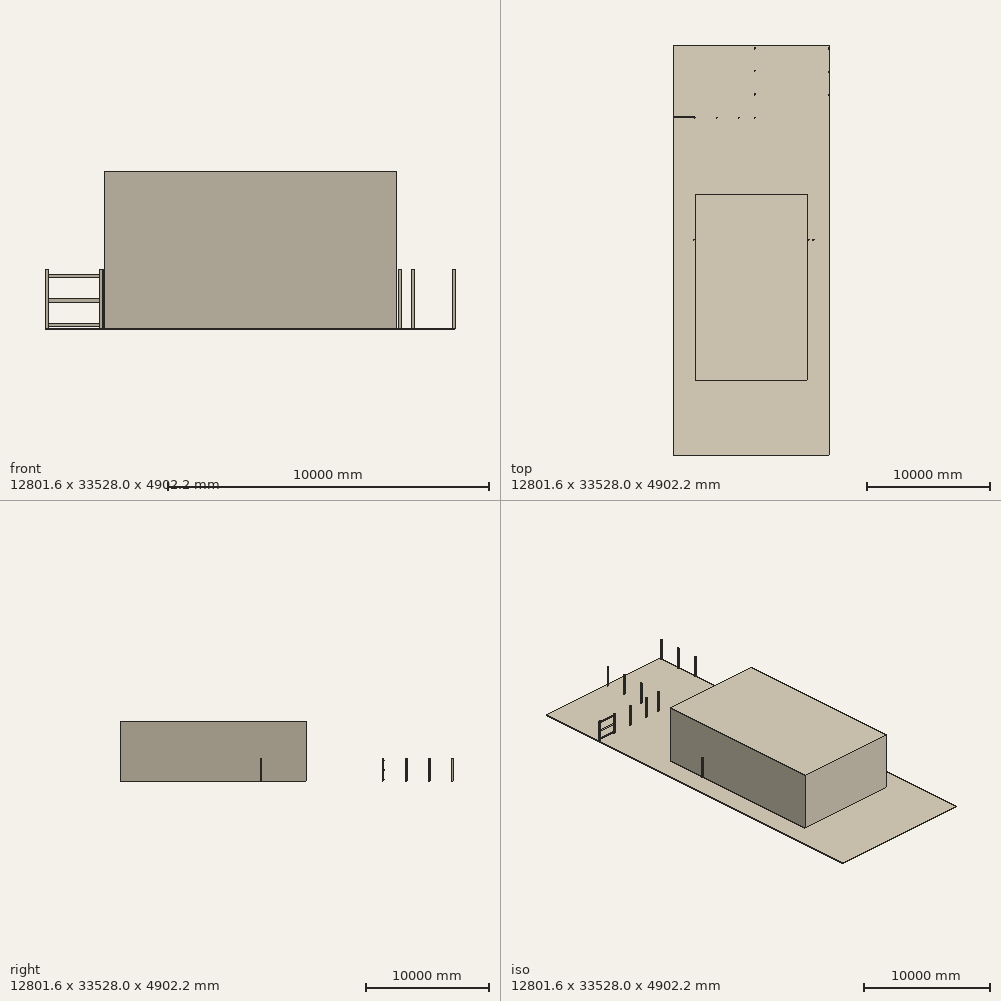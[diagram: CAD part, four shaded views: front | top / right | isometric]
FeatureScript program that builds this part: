
annotation { "Feature Type Name" : "Feature", "Feature Type Description" : "" }
export const myFeature = defineFeature(function(context is Context, id is Id, definition is map)
    precondition{}
    {
        {
            var Q0;
            Q0=qCreatedBy(makeId("Top.planeOp"),FACE);
            var sketch = newSketch(context, id + "F0", { "sketchPlane" : qUnion([Q0])});
            skLineSegment(sketch, "E0", {"start": v(-6400.8, 16764) * mm, "end": v(6400.8, 16764) * mm});
            skLineSegment(sketch, "E1", {"start": v(-6400.8, 16764) * mm, "end": v(-6400.8, -16764) * mm});
            skLineSegment(sketch, "E2", {"start": v(-6400.8, -16764) * mm, "end": v(6400.8, -16764) * mm});
            skLineSegment(sketch, "E3", {"start": v(6400.8, -16764) * mm, "end": v(6400.8, 16764) * mm});
            skLineSegment(sketch, "E4", {"start": v(0, -16764) * mm, "end": v(0, 16764) * mm, "construction": true});
            skSolve(sketch);
        }
        {
            var Q0;
            Q0 = qSketchRegion(id + "F0", true);
            extrude(context, id + "F1", {"entities" : qUnion([Q0]), "depth" : 25.4 * mm, "offsetDistance" : 25.4 * mm});
        }
        {
            var Q0;
            Q0=makeQuery(id+"F1.opExtrude","CAP_FACE",FACE,{"disambiguationData":[OSD([sQuery(id+"F0.wireOp",EDGE,"E0"),sQuery(id+"F0.wireOp",EDGE,"E1"),sQuery(id+"F0.wireOp",EDGE,"E2"),sQuery(id+"F0.wireOp",EDGE,"E3")])],"isStart":false});
            var sketch = newSketch(context, id + "F2", { "sketchPlane" : qUnion([Q0])});
            skLineSegment(sketch, "E5.bottom", {"start": v(-4572, 4572) * mm, "end": v(4572, 4572) * mm});
            skLineSegment(sketch, "E5.top", {"start": v(-4572, -10668) * mm, "end": v(4572, -10668) * mm});
            skLineSegment(sketch, "E5.left", {"start": v(-4572, 4572) * mm, "end": v(-4572, -10668) * mm});
            skLineSegment(sketch, "E5.right", {"start": v(4572, 4572) * mm, "end": v(4572, -10668) * mm});
            skSolve(sketch);
        }
        {
            var Q0;
            Q0 = qSketchRegion(id + "F2", true);
            extrude(context, id + "F3", {"entities" : qUnion([Q0]), "depth" : 4876.8 * mm, "offsetDistance" : 25.4 * mm});
        }
        {
            var Q0;
            Q0=makeQuery(id+"F1.opExtrude","CAP_FACE",FACE,{"disambiguationData":[OSD([sQuery(id+"F0.wireOp",EDGE,"E0"),sQuery(id+"F0.wireOp",EDGE,"E1"),sQuery(id+"F0.wireOp",EDGE,"E2"),sQuery(id+"F0.wireOp",EDGE,"E3")])],"isStart":false});
            var sketch = newSketch(context, id + "F4", { "sketchPlane" : qUnion([Q0])});
            skLineSegment(sketch, "E6.bottom", {"start": v(-6400.8, 10769.6) * mm, "end": v(-6299.2, 10769.6) * mm});
            skLineSegment(sketch, "E6.top", {"start": v(-6400.8, 10871.2) * mm, "end": v(-6299.2, 10871.2) * mm});
            skLineSegment(sketch, "E6.left", {"start": v(-6400.8, 10769.6) * mm, "end": v(-6400.8, 10871.2) * mm});
            skLineSegment(sketch, "E6.right", {"start": v(-6299.2, 10769.6) * mm, "end": v(-6299.2, 10871.2) * mm});
            skLineSegment(sketch, "E7.bottom", {"start": v(-4690.53, 10769.6) * mm, "end": v(-4588.93, 10769.6) * mm});
            skLineSegment(sketch, "E7.top", {"start": v(-4690.53, 10871.2) * mm, "end": v(-4588.93, 10871.2) * mm});
            skLineSegment(sketch, "E7.left", {"start": v(-4690.53, 10769.6) * mm, "end": v(-4690.53, 10871.2) * mm});
            skLineSegment(sketch, "E7.right", {"start": v(-4588.93, 10769.6) * mm, "end": v(-4588.93, 10871.2) * mm});
            skLineSegment(sketch, "E8.bottom", {"start": v(254, 10769.6) * mm, "end": v(355.6, 10769.6) * mm});
            skLineSegment(sketch, "E8.top", {"start": v(254, 10871.2) * mm, "end": v(355.6, 10871.2) * mm});
            skLineSegment(sketch, "E8.left", {"start": v(254, 10769.6) * mm, "end": v(254, 10871.2) * mm});
            skLineSegment(sketch, "E8.right", {"start": v(355.6, 10769.6) * mm, "end": v(355.6, 10871.2) * mm});
            skLineSegment(sketch, "E9.bottom", {"start": v(254, 14630.4) * mm, "end": v(355.6, 14630.4) * mm});
            skLineSegment(sketch, "E9.top", {"start": v(254, 14732) * mm, "end": v(355.6, 14732) * mm});
            skLineSegment(sketch, "E9.left", {"start": v(254, 14630.4) * mm, "end": v(254, 14732) * mm});
            skLineSegment(sketch, "E9.right", {"start": v(355.6, 14630.4) * mm, "end": v(355.6, 14732) * mm});
            skLineSegment(sketch, "E10", {"start": v(-6350, 10871.2) * mm, "end": v(-4639.73, 10871.2) * mm, "construction": true});
            skLineSegment(sketch, "E11", {"start": v(304.8, 10871.2) * mm, "end": v(304.8, 12700) * mm, "construction": true});
            skLineSegment(sketch, "E12.bottom", {"start": v(6299.2, 16459.2) * mm, "end": v(6400.8, 16459.2) * mm});
            skLineSegment(sketch, "E12.top", {"start": v(6299.2, 16560.8) * mm, "end": v(6400.8, 16560.8) * mm});
            skLineSegment(sketch, "E12.left", {"start": v(6299.2, 16459.2) * mm, "end": v(6299.2, 16560.8) * mm});
            skLineSegment(sketch, "E12.right", {"start": v(6400.8, 16459.2) * mm, "end": v(6400.8, 16560.8) * mm});
            skLineSegment(sketch, "E13", {"start": v(355.6, 16459.2) * mm, "end": v(6350, 16459.2) * mm, "construction": true});
            skLineSegment(sketch, "E14.bottom", {"start": v(254, 16459.2) * mm, "end": v(355.6, 16459.2) * mm});
            skLineSegment(sketch, "E14.top", {"start": v(254, 16560.8) * mm, "end": v(355.6, 16560.8) * mm});
            skLineSegment(sketch, "E14.left", {"start": v(254, 16459.2) * mm, "end": v(254, 16560.8) * mm});
            skLineSegment(sketch, "E14.right", {"start": v(355.6, 16459.2) * mm, "end": v(355.6, 16560.8) * mm});
            skLineSegment(sketch, "E15", {"start": v(304.8, 14732) * mm, "end": v(304.8, 16560.8) * mm, "construction": true});
            skLineSegment(sketch, "E16.bottom", {"start": v(5029.2, 812.8) * mm, "end": v(5130.8, 812.8) * mm});
            skLineSegment(sketch, "E16.top", {"start": v(5029.2, 914.4) * mm, "end": v(5130.8, 914.4) * mm});
            skLineSegment(sketch, "E16.left", {"start": v(5029.2, 812.8) * mm, "end": v(5029.2, 914.4) * mm});
            skLineSegment(sketch, "E16.right", {"start": v(5130.8, 812.8) * mm, "end": v(5130.8, 914.4) * mm});
            skLineSegment(sketch, "E17.bottom", {"start": v(4622.8, 812.8) * mm, "end": v(4724.4, 812.8) * mm});
            skLineSegment(sketch, "E17.top", {"start": v(4622.8, 914.4) * mm, "end": v(4724.4, 914.4) * mm});
            skLineSegment(sketch, "E17.left", {"start": v(4622.8, 812.8) * mm, "end": v(4622.8, 914.4) * mm});
            skLineSegment(sketch, "E17.right", {"start": v(4724.4, 812.8) * mm, "end": v(4724.4, 914.4) * mm});
            skLineSegment(sketch, "E18.bottom", {"start": v(6299.2, 812.8) * mm, "end": v(6400.8, 812.8) * mm, "construction": true});
            skLineSegment(sketch, "E18.top", {"start": v(6299.2, 914.4) * mm, "end": v(6400.8, 914.4) * mm, "construction": true});
            skLineSegment(sketch, "E18.left", {"start": v(6299.2, 812.8) * mm, "end": v(6299.2, 914.4) * mm, "construction": true});
            skLineSegment(sketch, "E18.right", {"start": v(6400.8, 812.8) * mm, "end": v(6400.8, 914.4) * mm, "construction": true});
            skLineSegment(sketch, "E19", {"start": v(4724.4, 914.4) * mm, "end": v(5029.2, 914.4) * mm, "construction": true});
            skLineSegment(sketch, "E20", {"start": v(5130.8, 914.4) * mm, "end": v(6299.2, 914.4) * mm, "construction": true});
            skLineSegment(sketch, "E21", {"start": v(0, 0) * mm, "end": v(0, 5689.72) * mm, "construction": true});
            skLineSegment(sketch, "E22.MirrorCS", {"start": v(-5130.8, 812.8) * mm, "end": v(-5130.8, 914.4) * mm, "construction": true});
            skLineSegment(sketch, "E23.MirrorCS", {"start": v(-4622.8, 914.4) * mm, "end": v(-4724.4, 914.4) * mm});
            skLineSegment(sketch, "E24.MirrorCS", {"start": v(-4622.8, 812.8) * mm, "end": v(-4724.4, 812.8) * mm});
            skLineSegment(sketch, "E25.MirrorCS", {"start": v(-6400.8, 812.8) * mm, "end": v(-6400.8, 914.4) * mm, "construction": true});
            skLineSegment(sketch, "E26.MirrorCS", {"start": v(-5029.2, 812.8) * mm, "end": v(-5029.2, 914.4) * mm, "construction": true});
            skLineSegment(sketch, "E27.MirrorCS", {"start": v(-4724.4, 812.8) * mm, "end": v(-4724.4, 914.4) * mm});
            skLineSegment(sketch, "E28.MirrorCS", {"start": v(-6299.2, 914.4) * mm, "end": v(-6400.8, 914.4) * mm, "construction": true});
            skLineSegment(sketch, "E29.MirrorCS", {"start": v(-6299.2, 812.8) * mm, "end": v(-6299.2, 914.4) * mm, "construction": true});
            skLineSegment(sketch, "E30.MirrorCS", {"start": v(-5130.8, 914.4) * mm, "end": v(-6299.2, 914.4) * mm, "construction": true});
            skLineSegment(sketch, "E31.MirrorCS", {"start": v(-5029.2, 812.8) * mm, "end": v(-5130.8, 812.8) * mm, "construction": true});
            skLineSegment(sketch, "E32.MirrorCS", {"start": v(-4622.8, 812.8) * mm, "end": v(-4622.8, 914.4) * mm});
            skLineSegment(sketch, "E33.MirrorCS", {"start": v(-5029.2, 914.4) * mm, "end": v(-5130.8, 914.4) * mm, "construction": true});
            skLineSegment(sketch, "E34.MirrorCS", {"start": v(-6299.2, 812.8) * mm, "end": v(-6400.8, 812.8) * mm, "construction": true});
            skLineSegment(sketch, "E35.MirrorCS", {"start": v(-4724.4, 914.4) * mm, "end": v(-5029.2, 914.4) * mm, "construction": true});
            skLineSegment(sketch, "E36.bottom", {"start": v(6400.8, 14562.67) * mm, "end": v(6299.2, 14562.67) * mm});
            skLineSegment(sketch, "E36.top", {"start": v(6400.8, 14664.27) * mm, "end": v(6299.2, 14664.27) * mm});
            skLineSegment(sketch, "E36.left", {"start": v(6400.8, 14562.67) * mm, "end": v(6400.8, 14664.27) * mm});
            skLineSegment(sketch, "E36.right", {"start": v(6299.2, 14562.67) * mm, "end": v(6299.2, 14664.27) * mm});
            skLineSegment(sketch, "E37", {"start": v(6350, 14664.27) * mm, "end": v(6350, 16459.2) * mm, "construction": true});
            skLineSegment(sketch, "E38", {"start": v(6350, 14562.67) * mm, "end": v(6350, 12767.73) * mm, "construction": true});
            skLineSegment(sketch, "E39.bottom", {"start": v(6400.8, 12666.13) * mm, "end": v(6299.2, 12666.13) * mm});
            skLineSegment(sketch, "E39.top", {"start": v(6400.8, 12767.73) * mm, "end": v(6299.2, 12767.73) * mm});
            skLineSegment(sketch, "E39.left", {"start": v(6400.8, 12666.13) * mm, "end": v(6400.8, 12767.73) * mm});
            skLineSegment(sketch, "E39.right", {"start": v(6299.2, 12666.13) * mm, "end": v(6299.2, 12767.73) * mm});
            skLineSegment(sketch, "E40", {"start": v(6350, 12666.13) * mm, "end": v(6350, 10871.2) * mm, "construction": true});
            skLineSegment(sketch, "E41.bottom", {"start": v(254, 12801.6) * mm, "end": v(355.6, 12801.6) * mm});
            skLineSegment(sketch, "E41.top", {"start": v(254, 12700) * mm, "end": v(355.6, 12700) * mm});
            skLineSegment(sketch, "E41.left", {"start": v(254, 12801.6) * mm, "end": v(254, 12700) * mm});
            skLineSegment(sketch, "E41.right", {"start": v(355.6, 12801.6) * mm, "end": v(355.6, 12700) * mm});
            skPoint(sketch, "E42.orphan", {"position": v(304.8, 14732) * mm});
            skLineSegment(sketch, "E43.trimOffspring", {"start": v(304.8, 12801.6) * mm, "end": v(304.8, 14630.4) * mm, "construction": true});
            skLineSegment(sketch, "E44.bottom", {"start": v(-1066.8, 10871.2) * mm, "end": v(-965.2, 10871.2) * mm});
            skLineSegment(sketch, "E44.top", {"start": v(-1066.8, 10769.6) * mm, "end": v(-965.2, 10769.6) * mm});
            skLineSegment(sketch, "E44.left", {"start": v(-1066.8, 10871.2) * mm, "end": v(-1066.8, 10769.6) * mm});
            skLineSegment(sketch, "E44.right", {"start": v(-965.2, 10871.2) * mm, "end": v(-965.2, 10769.6) * mm});
            skLineSegment(sketch, "E45.bottom", {"start": v(-2878.67, 10871.2) * mm, "end": v(-2777.07, 10871.2) * mm});
            skLineSegment(sketch, "E45.top", {"start": v(-2878.67, 10769.6) * mm, "end": v(-2777.07, 10769.6) * mm});
            skLineSegment(sketch, "E45.left", {"start": v(-2878.67, 10871.2) * mm, "end": v(-2878.67, 10769.6) * mm});
            skLineSegment(sketch, "E45.right", {"start": v(-2777.07, 10871.2) * mm, "end": v(-2777.07, 10769.6) * mm});
            skLineSegment(sketch, "E46", {"start": v(-4588.93, 10871.2) * mm, "end": v(-2878.67, 10871.2) * mm, "construction": true});
            skLineSegment(sketch, "E47", {"start": v(-2777.07, 10871.2) * mm, "end": v(-1066.8, 10871.2) * mm, "construction": true});
            skPoint(sketch, "E48", {"position": v(-2827.87, 10871.2) * mm});
            skPoint(sketch, "E49", {"position": v(-1016, 10871.2) * mm});
            skLineSegment(sketch, "E50", {"start": v(-965.2, 10871.2) * mm, "end": v(254, 10871.2) * mm, "construction": true});
            skSolve(sketch);
        }
        {
            var Q0;
            Q0 = qSketchRegion(id + "F4", true);
            extrude(context, id + "F5", {"entities" : qUnion([Q0]), "depth" : 1828.8 * mm, "offsetDistance" : 25.4 * mm});
        }
        {
            var Q0;
            Q0=makeQuery(id+"F5.opExtrude","SWEPT_FACE",FACE,{"disambiguationData":[OSD([sQuery(id+"F4.wireOp",EDGE,"E7.top")])]});
            var sketch = newSketch(context, id + "F6", { "sketchPlane" : qUnion([Q0])});
            skLineSegment(sketch, "E51.bottom", {"start": v(6350, 177.8) * mm, "end": v(4639.73, 177.8) * mm});
            skLineSegment(sketch, "E51.top", {"start": v(6350, 76.2) * mm, "end": v(4639.73, 76.2) * mm});
            skLineSegment(sketch, "E51.left", {"start": v(6350, 177.8) * mm, "end": v(6350, 76.2) * mm});
            skLineSegment(sketch, "E51.right", {"start": v(4639.73, 177.8) * mm, "end": v(4639.73, 76.2) * mm});
            skLineSegment(sketch, "E52.bottom", {"start": v(6350, 1701.8) * mm, "end": v(4639.73, 1701.8) * mm});
            skLineSegment(sketch, "E52.top", {"start": v(6350, 1600.2) * mm, "end": v(4639.73, 1600.2) * mm});
            skLineSegment(sketch, "E52.left", {"start": v(6350, 1701.8) * mm, "end": v(6350, 1600.2) * mm});
            skLineSegment(sketch, "E52.right", {"start": v(4639.73, 1701.8) * mm, "end": v(4639.73, 1600.2) * mm});
            skLineSegment(sketch, "E53", {"start": v(6350, 1854.2) * mm, "end": v(6350, 118.08) * mm, "construction": true});
            skLineSegment(sketch, "E54", {"start": v(4639.73, 1854.2) * mm, "end": v(4639.73, 25.4) * mm, "construction": true});
            skLineSegment(sketch, "E55.bottom", {"start": v(4639.73, 939.8) * mm, "end": v(6350, 939.8) * mm});
            skLineSegment(sketch, "E55.top", {"start": v(4639.73, 838.2) * mm, "end": v(6350, 838.2) * mm});
            skLineSegment(sketch, "E55.left", {"start": v(4639.73, 939.8) * mm, "end": v(4639.73, 838.2) * mm});
            skLineSegment(sketch, "E55.right", {"start": v(6350, 939.8) * mm, "end": v(6350, 838.2) * mm});
            skLineSegment(sketch, "E56", {"start": v(5494.87, 177.8) * mm, "end": v(5494.87, 838.2) * mm, "construction": true});
            skLineSegment(sketch, "E57", {"start": v(5494.87, 939.8) * mm, "end": v(5494.87, 1600.2) * mm, "construction": true});
            skSolve(sketch);
        }
        {
            var Q0;
            Q0 = qSketchRegion(id + "F6", true);
            extrude(context, id + "F7", {"entities" : qUnion([Q0]), "depth" : 50.8 * mm, "offsetDistance" : 25.4 * mm});
        }
    });
